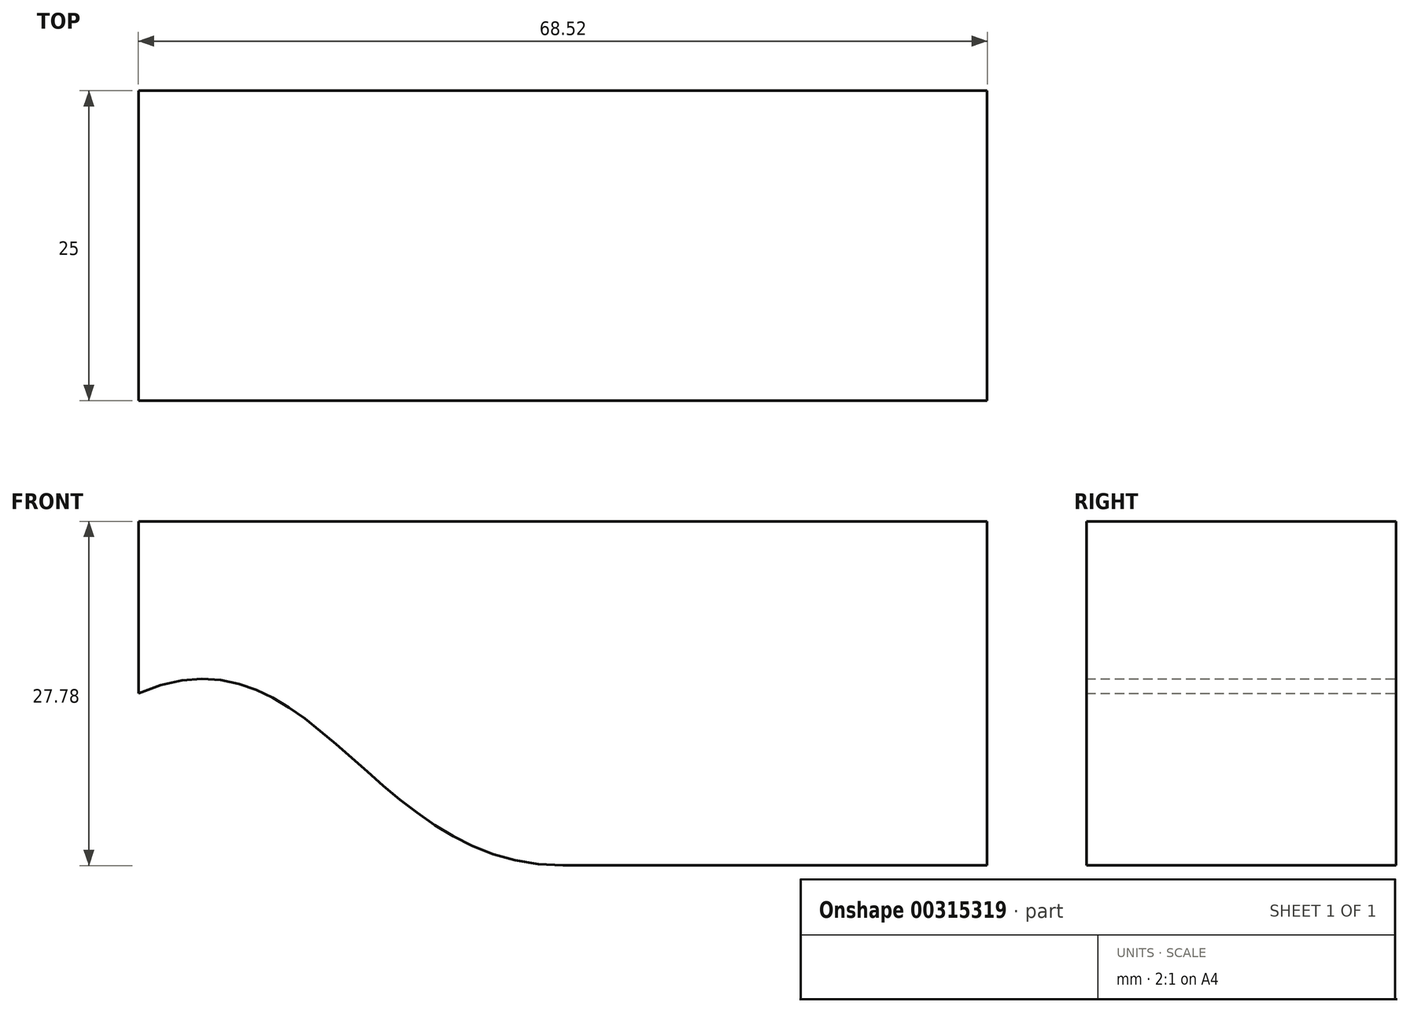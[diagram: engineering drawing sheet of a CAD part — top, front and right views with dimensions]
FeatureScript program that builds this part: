
annotation { "Feature Type Name" : "Feature", "Feature Type Description" : "" }
export const myFeature = defineFeature(function(context is Context, id is Id, definition is map)
    precondition{}
    {
        {
            var Q0;
            Q0=qCreatedBy(makeId("Front.planeOp"),FACE);
            var sketch = newSketch(context, id + "F0", { "sketchPlane" : qUnion([Q0])});
            skLineSegment(sketch, "E0.bottom", {"start": v(34.26, -13.89) * mm, "end": v(-34.26, -13.89) * mm});
            skLineSegment(sketch, "E0.top", {"start": v(34.26, 13.89) * mm, "end": v(-34.26, 13.89) * mm});
            skLineSegment(sketch, "E0.left", {"start": v(34.26, -13.89) * mm, "end": v(34.26, 13.89) * mm});
            skLineSegment(sketch, "E0.right", {"start": v(-34.26, -13.89) * mm, "end": v(-34.26, 13.89) * mm});
            skPoint(sketch, "E0.middle", {"position": v(0, 0) * mm});
            skFitSpline(sketch, "E1", {"points": [v(-34.26, 0) * mm, v(0, -13.89) * mm], "startDerivative": vector(42.74, 18.44) * mm, "endDerivative": vector(47.16, 0) * mm});
            skSolve(sketch);
        }
        {
            var Q0;
            {var subQ1=sQuery(id+"F0.wireOp",EDGE,"E0.top");Q0=makeQuery(id+"F0.imprint","IMPRINT",FACE,{"disambiguationData":[TD([[makeQuery(id+"F0.imprint","IMPRINT",EDGE,{"derivedFrom":subQ1}),1.0]])]});}
            extrude(context, id + "F1", {"entities" : qUnion([Q0]), "depth" : 25 * mm});
        }
    });
